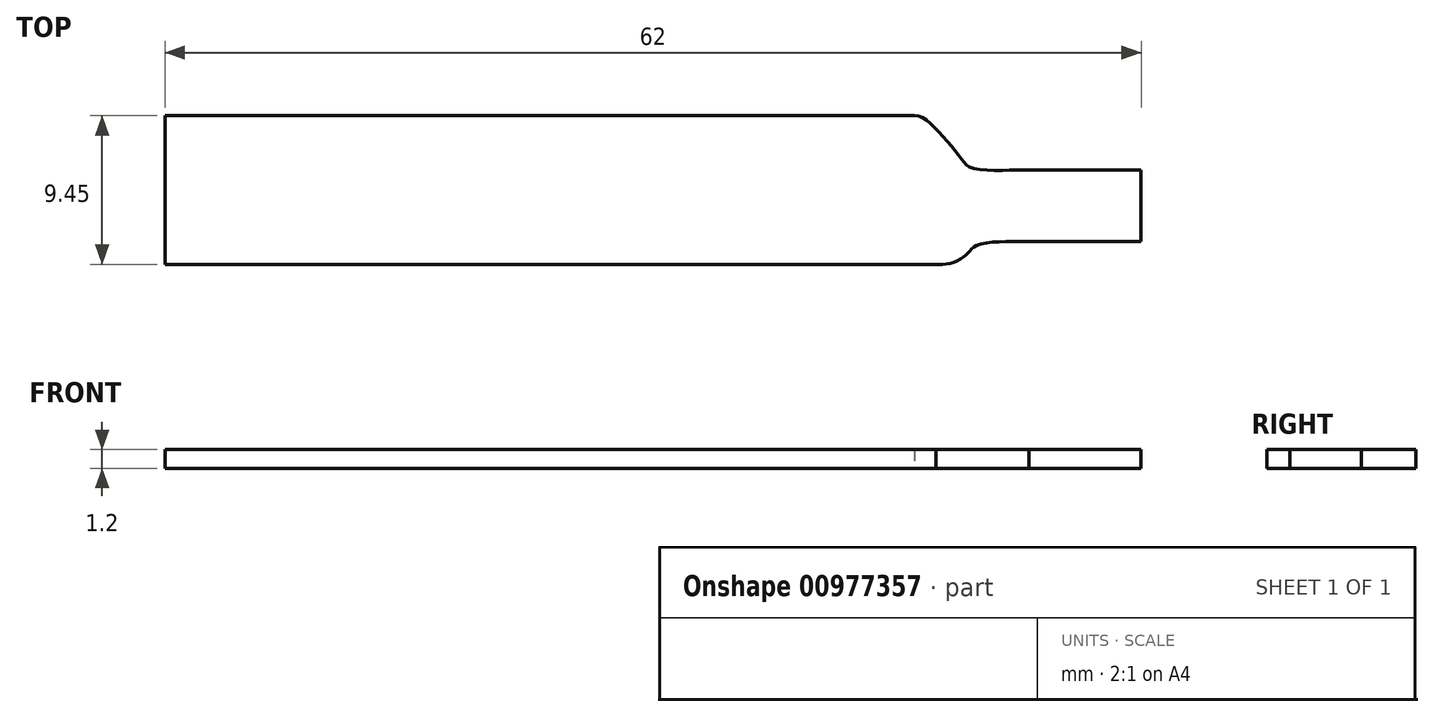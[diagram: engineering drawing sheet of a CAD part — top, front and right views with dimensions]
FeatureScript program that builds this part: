
annotation { "Feature Type Name" : "Feature", "Feature Type Description" : "" }
export const myFeature = defineFeature(function(context is Context, id is Id, definition is map)
    precondition{}
    {
        {
            var Q0;
            Q0=qCreatedBy(makeId("Top.planeOp"),FACE);
            var sketch = newSketch(context, id + "F0", { "sketchPlane" : qUnion([Q0])});
            skLineSegment(sketch, "E0", {"start": v(-18.4, 0) * mm, "end": v(17.36, 0) * mm});
            skLineSegment(sketch, "E1", {"start": v(-18.4, 0) * mm, "end": v(-31.6, 0) * mm});
            skLineSegment(sketch, "E2", {"start": v(-31.6, 0) * mm, "end": v(-31.6, 9.45) * mm});
            skLineSegment(sketch, "E3", {"start": v(-31.6, 9.45) * mm, "end": v(16, 9.45) * mm});
            skFitSpline(sketch, "E4", {"points": [v(16, 9.45) * mm, v(17.3, 8.68) * mm, v(18.9, 6.8) * mm, v(19.76, 6.1) * mm, v(22.7, 6) * mm], "startDerivative": vector(6.16, 0.27) * mm, "endDerivative": vector(5, 0) * mm});
            skFitSpline(sketch, "E5", {"points": [v(17.36, 0) * mm, v(18.51, 0.15) * mm, v(19.42, 0.74) * mm, v(20.05, 1.25) * mm, v(23.27, 1.45) * mm], "startDerivative": vector(4.07, -0.2) * mm, "endDerivative": vector(5.24, -0.23) * mm});
            skLineSegment(sketch, "E6", {"start": v(22.7, 6) * mm, "end": v(30.4, 6) * mm});
            skLineSegment(sketch, "E7", {"start": v(30.4, 6) * mm, "end": v(30.4, 1.45) * mm});
            skLineSegment(sketch, "E8", {"start": v(30.4, 1.45) * mm, "end": v(23.27, 1.45) * mm});
            skSolve(sketch);
        }
        {
            var Q0;
            Q0=makeQuery(id+"F0.imprint","IMPRINT",FACE,{"disambiguationData":[TD([[makeQuery(id+"F0.imprint","IMPRINT",EDGE,{"derivedFrom":sQuery(id+"F0.wireOp",EDGE,"E0")}),1.0]])]});
            extrude(context, id + "F1", {"entities" : qUnion([Q0]), "depth" : 1.2 * mm, "offsetDistance" : 25 * mm});
        }
    });
